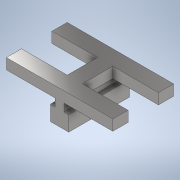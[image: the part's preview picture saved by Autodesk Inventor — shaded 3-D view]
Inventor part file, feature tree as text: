
AUTODESK INVENTOR PART (.ipt)
format: ipt  version: 2022 (Build 260153000, 153)  size: 161,792 bytes
history: native  units: in
note: dims shown in document units (in); Inventor stores cm internally (conversion verified against a paired STEP export)
features: extrude x2, sketch x2
ambient origin geometry x8: Origin, YZ Plane, XZ Plane, XY Plane, X Axis, Y Axis, Z Axis, Center Point
bodies: Solid1 (feature_tree)
feature tree (4):
  extrude  "Extrusion1"  Depth=3.937in
  extrude  "Extrusion2"  Depth=7.874in
  sketch  "Sketch1"  dims[d0=27.5591in d1=3.937in]
  sketch  "Sketch2"  dims[d2=11.811in d3=7.874in d4=3.937in d5=27.5591in d6=11.811in d7=2.7559in d8=0.0in d9=1.1811in d10=2.3622in d11=1.9685in d12=1.1811in d13=3.937in d14=4.7244in d15=1.1811in d16=15.748in d17=0.0in]
